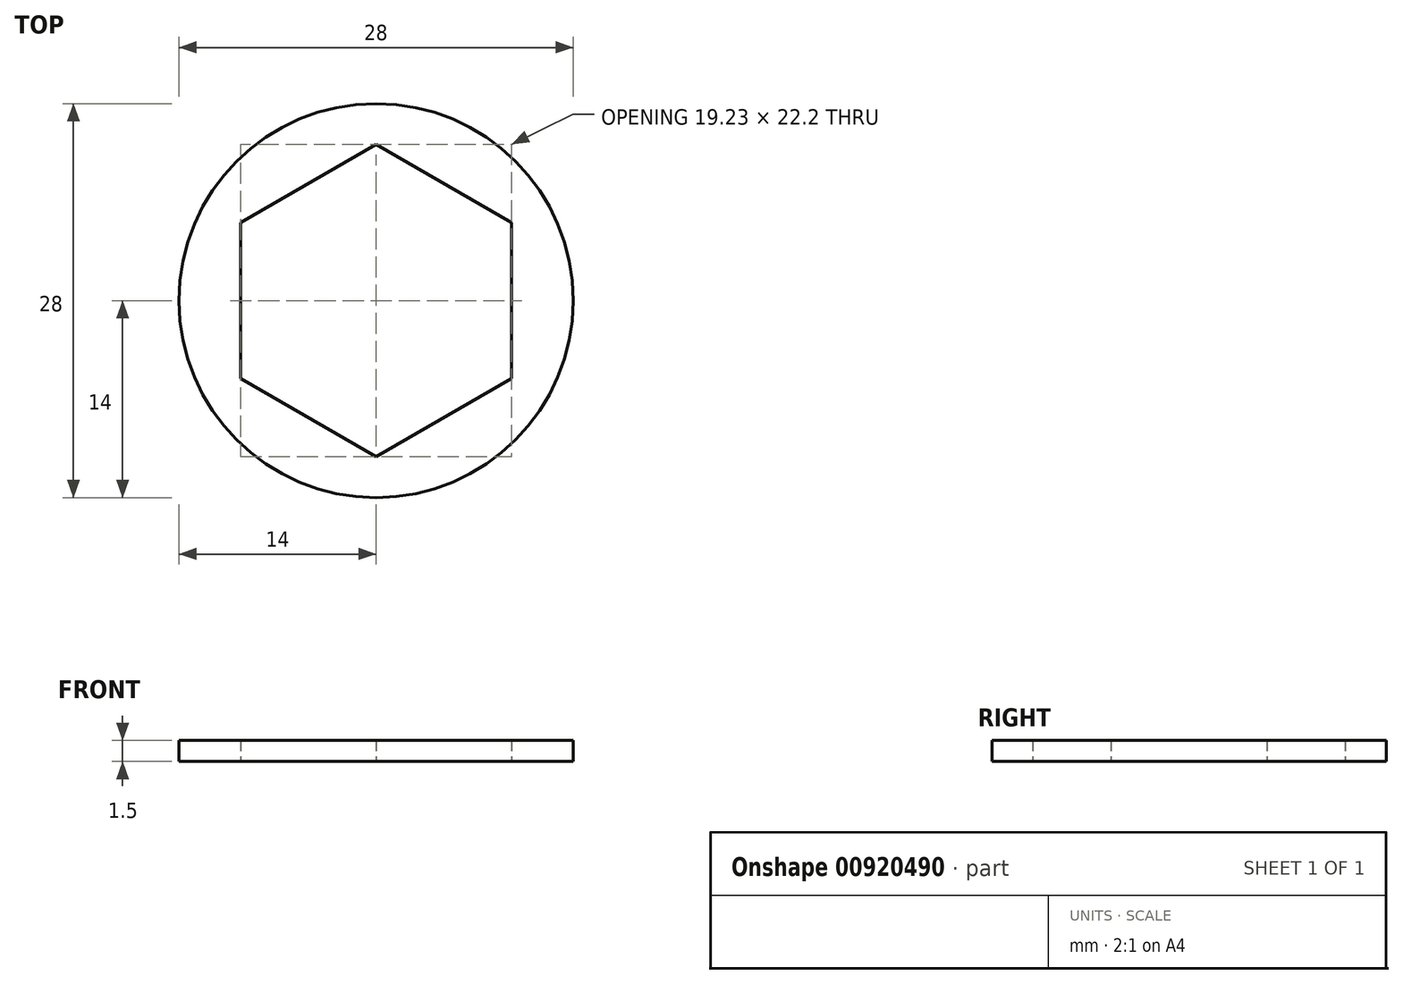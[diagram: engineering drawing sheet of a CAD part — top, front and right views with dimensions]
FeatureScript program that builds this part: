
annotation { "Feature Type Name" : "Feature", "Feature Type Description" : "" }
export const myFeature = defineFeature(function(context is Context, id is Id, definition is map)
    precondition{}
    {
        {
            var Q0;
            Q0=qCreatedBy(makeId("Top.planeOp"), FACE);
            var sketch = newSketch(context, id + "F0", { "sketchPlane" : qUnion([Q0])});
            skLineSegment(sketch, "E0", {"start": v(-9.61, 0) * mm, "end": v(-9.61, 5.55) * mm});
            skLineSegment(sketch, "E1", {"start": v(-9.61, 5.55) * mm, "end": v(0, 11.1) * mm});
            skLineSegment(sketch, "E2.MirrorCS", {"start": v(9.61, 5.55) * mm, "end": v(0, 11.1) * mm});
            skLineSegment(sketch, "E3.MirrorCS", {"start": v(9.61, 0) * mm, "end": v(9.61, 5.55) * mm});
            skLineSegment(sketch, "E4.MirrorCS", {"start": v(-9.61, 0) * mm, "end": v(-9.61, -5.55) * mm});
            skLineSegment(sketch, "E5.MirrorCS", {"start": v(-9.61, -5.55) * mm, "end": v(0, -11.1) * mm});
            skLineSegment(sketch, "E6.MirrorCS", {"start": v(9.61, -5.55) * mm, "end": v(0, -11.1) * mm});
            skLineSegment(sketch, "E7.MirrorCS", {"start": v(9.61, 0) * mm, "end": v(9.61, -5.55) * mm});
            skCircle(sketch, "E8", {"center": v(0, 0) * mm, "radius": 14 * mm});
            skSolve(sketch);
        }
        {
            var Q0;
            Q0 = qSketchRegion(id + "F0", true);
            extrude(context, id + "F1", {"entities" : qUnion([Q0]), "depth" : 1.5 * mm, "offsetDistance" : 25 * mm});
        }
    });
